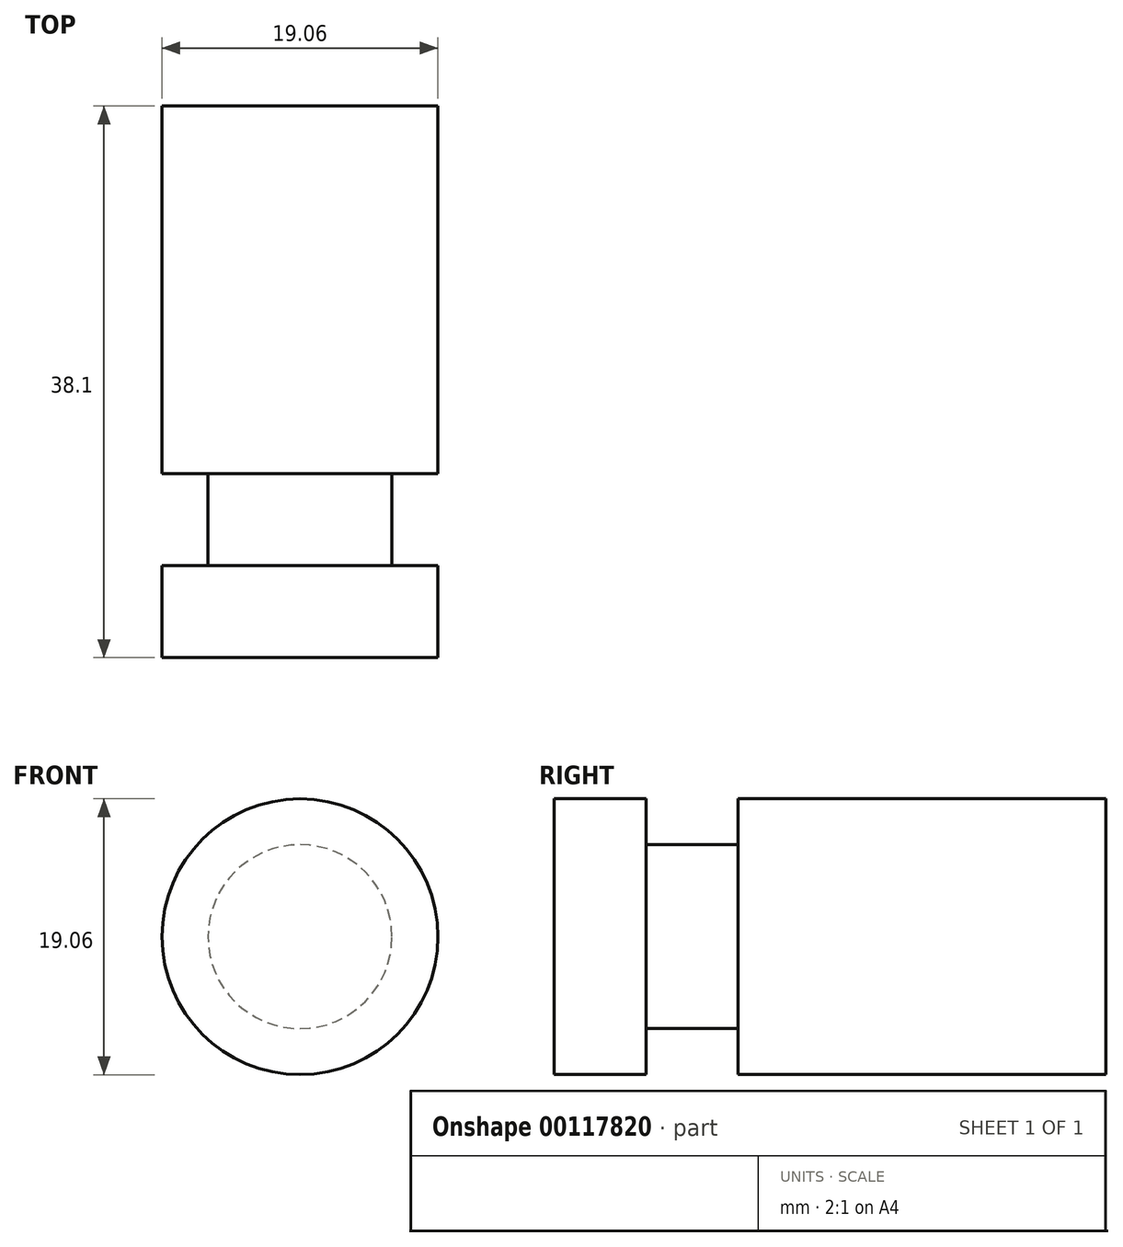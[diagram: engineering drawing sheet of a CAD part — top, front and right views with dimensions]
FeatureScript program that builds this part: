
annotation { "Feature Type Name" : "Feature", "Feature Type Description" : "" }
export const myFeature = defineFeature(function(context is Context, id is Id, definition is map)
    precondition{}
    {
        {
            var Q0;
            Q0=qCreatedBy(makeId("Right.planeOp"),FACE);
            var sketch = newSketch(context, id + "F0", { "sketchPlane" : qUnion([Q0])});
            skLineSegment(sketch, "E0", {"start": v(-18.58, 0) * mm, "end": v(-18.58, 9.53) * mm});
            skLineSegment(sketch, "E1", {"start": v(-18.58, 9.53) * mm, "end": v(-12.23, 9.53) * mm});
            skLineSegment(sketch, "E2", {"start": v(-12.23, 9.53) * mm, "end": v(-12.23, 6.35) * mm});
            skLineSegment(sketch, "E3", {"start": v(-12.23, 6.35) * mm, "end": v(-5.88, 6.35) * mm});
            skLineSegment(sketch, "E4", {"start": v(-5.88, 6.35) * mm, "end": v(-5.88, 9.52) * mm});
            skLineSegment(sketch, "E5", {"start": v(-5.88, 9.52) * mm, "end": v(19.52, 9.52) * mm});
            skLineSegment(sketch, "E6", {"start": v(19.52, 9.52) * mm, "end": v(19.52, 0) * mm});
            skLineSegment(sketch, "E7", {"start": v(-23.83, 0) * mm, "end": v(26.6, 0) * mm, "construction": true});
            skLineSegment(sketch, "E8", {"start": v(-18.58, 0) * mm, "end": v(19.52, 0) * mm});
            skSolve(sketch);
        }
        {
            var Q0;
            Q0 = qSketchRegion(id + "F0", true);
            var Q1;
            Q1=sQuery(id+"F0.wireOp",EDGE,"E7");
            revolve(context, id + "F1", {"entities" : qUnion([Q0]), "axis" : qUnion([Q1]), "revolveType" : RevolveType.FULL});
        }
    });
